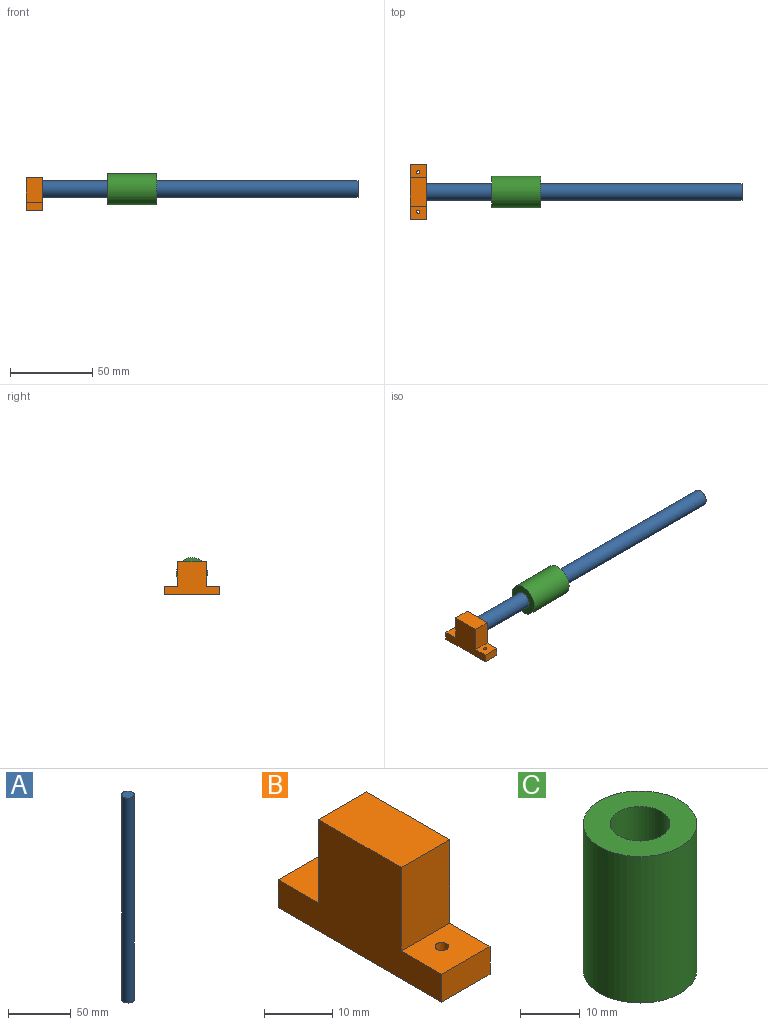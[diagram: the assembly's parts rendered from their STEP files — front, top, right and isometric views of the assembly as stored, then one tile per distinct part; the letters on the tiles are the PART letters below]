
ASSEMBLY  parts=3 mates=2
PART A: 3 faces, bbox 10x10x200 mm
  f0: cylinder r=5mm len=200mm, axis (0,0,-1), area 6283.2mm2, adj f1,f2
  f1: plane 10x10mm, normal (0,0,1), area 78.5mm2, adj f0
  f2: plane 10x10mm, normal (0,0,-1), area 78.5mm2, adj f0
PART B: 14 faces, bbox 10x34x20 mm
  f0: plane 10x8.39mm, normal (0,0,1), area 80.7mm2, adj f1,f3,f5,f6,f10
  f1: plane 34x20mm, normal (1,0,0), area 346.6mm2, adj f0,f2,f5,f7,f8,f9,f10,f11
  f2: plane 10x5mm, normal (0,1,0), area 50mm2, adj f1,f3,f7,f8
  f3: plane 34x20mm, normal (-1,0,0), area 428.4mm2, adj f0,f2,f5,f7,f8,f9,f10,f11
  f4: cylinder r=1mm len=5mm, axis (0,0,-1), area 31.4mm2, adj f7,f8
  f5: plane 10x5mm, normal (0,-1,0), area 50mm2, adj f0,f1,f3,f8
  f6: cylinder r=1mm len=5mm, axis (0,0,-1), area 31.4mm2, adj f0,f8
  f7: plane 10x8.39mm, normal (0,0,1), area 80.7mm2, adj f1,f2,f3,f4,f9
  f8: plane 34x10mm, normal (0,0,-1), area 333.7mm2, adj f1,f2,f3,f4,f5,f6
  f9: plane 15x10mm, normal (0,1,0), area 150mm2, adj f1,f3,f7,f11
  f10: plane 15x10mm, normal (0,-1,0), area 150mm2, adj f0,f1,f3,f11
  f11: plane 17.22x10mm, normal (0,0,1), area 172.2mm2, adj f1,f3,f9,f10
  f12: cylinder r=5.1mm len=10.2mm, axis (1,0,0), area 256.4mm2, adj f1,f13
  f13: plane 10.2x10.2mm, normal (1,0,0), area 81.7mm2, adj f12
PART C: 4 faces, bbox 19x19x30 mm
  f0: cylinder r=5mm len=30mm, axis (0,0,-1), area 942.5mm2, adj f2,f3
  f1: cylinder r=9.5mm len=30mm, axis (0,0,-1), area 1790.7mm2, adj f2,f3
  f2: plane 19x19mm, normal (0,0,1), area 205mm2, adj f0,f1
  f3: plane 19x19mm, normal (0,0,-1), area 205mm2, adj f0,f1
PLACE A rot(axis=(0.71,0,0.71),180deg) t=(-3,0,13)mm
PLACE B at identity fixed
PLACE C rot(axis=(0.58,0.58,0.58),120deg) t=(44.64,0,13)mm
MATE fastened B.f12 <-> A.f0  axis (1,0,0) through (-3,0,13)mm
MATE slider A.f0 <-> C.f0  axis (-1,0,0) through (97,0,13)mm
